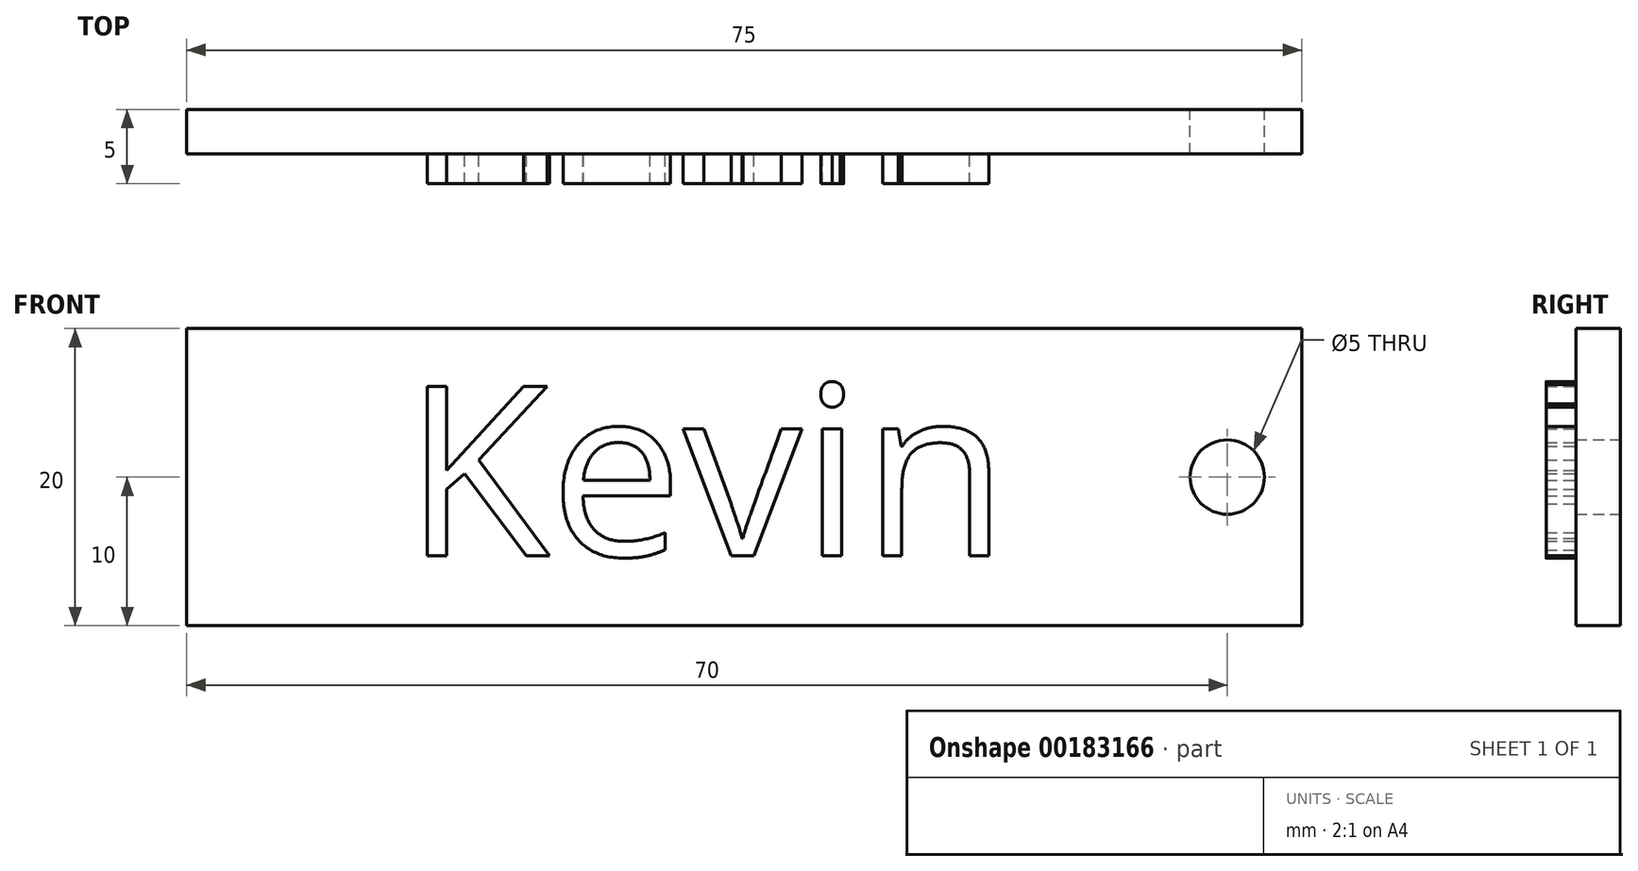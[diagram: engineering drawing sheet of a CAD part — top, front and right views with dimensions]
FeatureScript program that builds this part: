
annotation { "Feature Type Name" : "Feature", "Feature Type Description" : "" }
export const myFeature = defineFeature(function(context is Context, id is Id, definition is map)
    precondition{}
    {
        {
            var Q0;
            Q0=qCreatedBy(makeId("Front.planeOp"),FACE);
            var sketch = newSketch(context, id + "F0", { "sketchPlane" : qUnion([Q0])});
            skLineSegment(sketch, "E0.bottom", {"start": v(0, 0) * mm, "end": v(75, 0) * mm});
            skLineSegment(sketch, "E0.top", {"start": v(0, -20) * mm, "end": v(75, -20) * mm});
            skLineSegment(sketch, "E0.left", {"start": v(0, 0) * mm, "end": v(0, -20) * mm});
            skLineSegment(sketch, "E0.right", {"start": v(75, 0) * mm, "end": v(75, -20) * mm});
            skCircle(sketch, "E1", {"center": v(70, -10) * mm, "radius": 2.5 * mm});
            skSolve(sketch);
        }
        {
            var Q0;
            Q0 = qSketchRegion(id + "F0", true);
            extrude(context, id + "F1", {"entities" : qUnion([Q0]), "depth" : 3 * mm});
        }
        {
            var Q0;
            Q0=makeQuery(id+"F1.opExtrude","CAP_FACE",FACE,{"disambiguationData":[OSD([sQuery(id+"F0.wireOp",EDGE,"E0.bottom"),sQuery(id+"F0.wireOp",EDGE,"E0.top"),sQuery(id+"F0.wireOp",EDGE,"E0.left"),sQuery(id+"F0.wireOp",EDGE,"E0.right"),sQuery(id+"F0.wireOp",EDGE,"E1")])],"isStart":false});
            var sketch = newSketch(context, id + "F2", { "sketchPlane" : qUnion([Q0])});
            skText(sketch, "E2", { "text": "Kevin\n", "fontName": "OpenSans-Regular.ttf"});
            const initialGuessF2  = {"E2": [0.0146, -0.0153, 1, 0, 0.01151]};
            skSetInitialGuess(sketch, initialGuessF2);
            skSolve(sketch);
        }
        {
            var Q0;
            Q0 = qSketchRegion(id + "F2", true);
            extrude(context, id + "F3", {"entities" : qUnion([Q0]), "operationType" : NewBodyOperationType.ADD, "depth" : 2 * mm});
        }
    });
